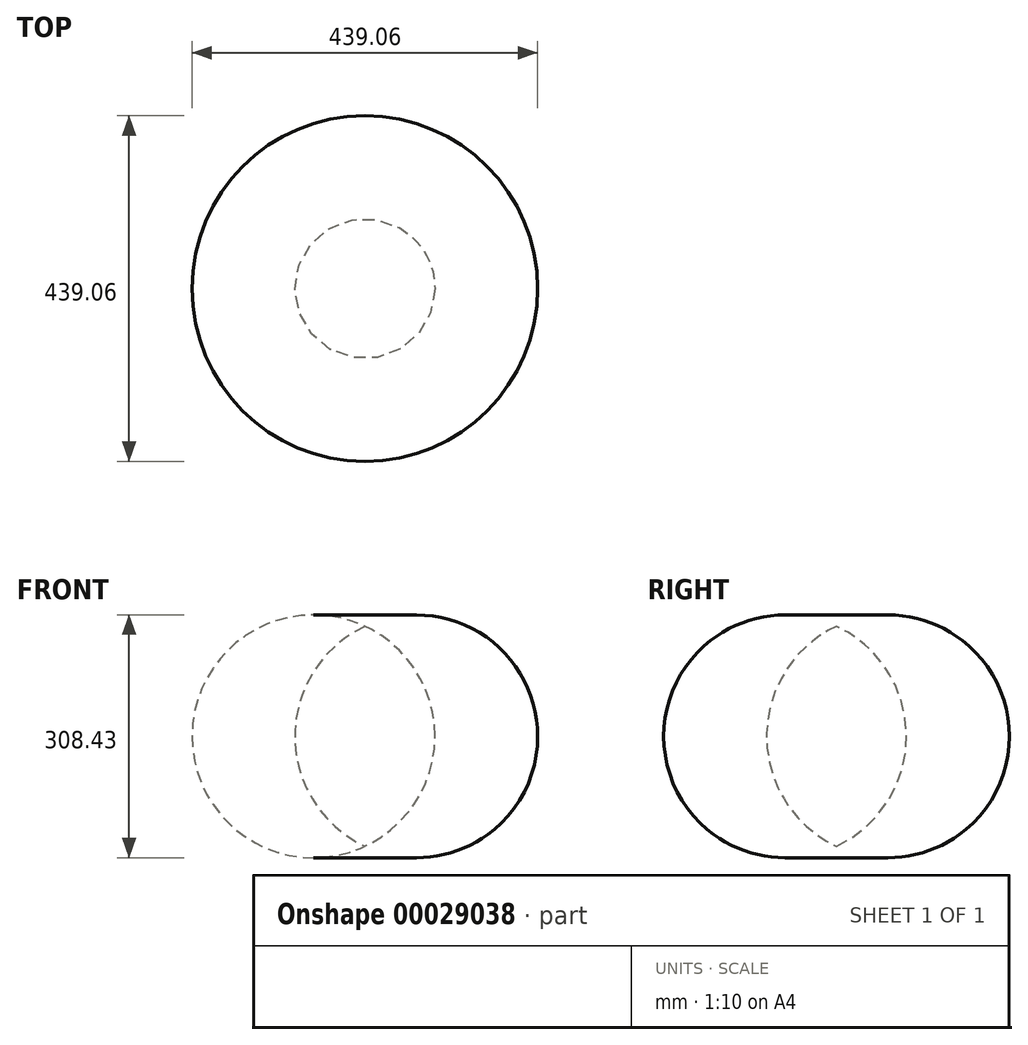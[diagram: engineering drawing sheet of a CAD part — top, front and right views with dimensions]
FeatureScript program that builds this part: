
annotation { "Feature Type Name" : "Feature", "Feature Type Description" : "" }
export const myFeature = defineFeature(function(context is Context, id is Id, definition is map)
    precondition{}
    {
        {
            var Q0;
            Q0=qCreatedBy(makeId("Front.planeOp"),FACE);
            var sketch = newSketch(context, id + "F0", { "sketchPlane" : qUnion([Q0])});
            skLineSegment(sketch, "E0", {"start": v(0, -121.61) * mm, "end": v(0, 157.79) * mm});
            skArc(sketch, "E1", {"start": v(0, -121.61) * mm, "mid": v(88.9, 18.09) * mm, "end": v(0, 157.79) * mm});
            skSolve(sketch);
        }
        {
            var Q0;
            Q0=makeQuery(id+"F0.imprint","IMPRINT",FACE,{"disambiguationData":[TD([[makeQuery(id+"F0.imprint","IMPRINT",EDGE,{"derivedFrom":sQuery(id+"F0.wireOp",EDGE,"E0")}),-1.0]])]});
            var Q1;
            Q1=sQuery(id+"F0.wireOp",EDGE,"E0");
            revolve(context, id + "F1", {"entities" : qUnion([Q0]), "axis" : qUnion([Q1]), "revolveType" : RevolveType.FULL});
        }
    });
